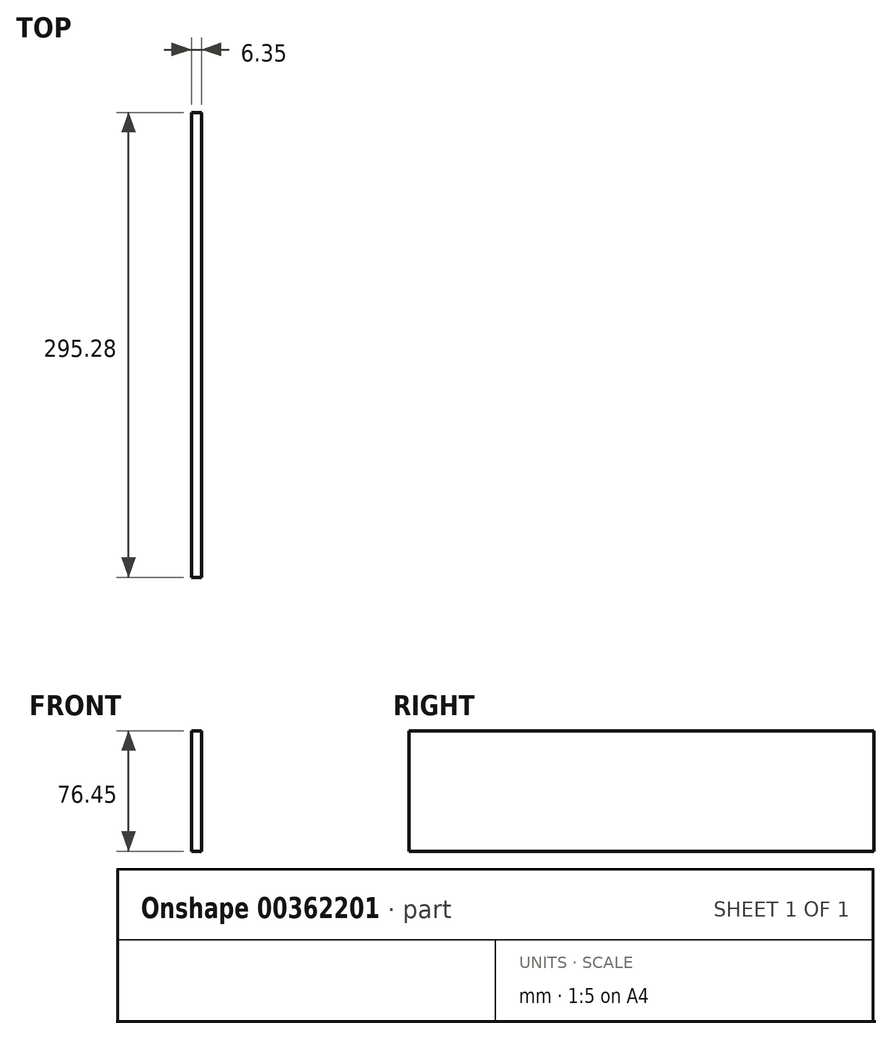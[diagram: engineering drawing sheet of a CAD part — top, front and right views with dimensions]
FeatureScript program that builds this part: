
annotation { "Feature Type Name" : "Feature", "Feature Type Description" : "" }
export const myFeature = defineFeature(function(context is Context, id is Id, definition is map)
    precondition{}
    {
        {
            var Q0;
            Q0=qCreatedBy(makeId("Right.planeOp"),FACE);
            var sketch = newSketch(context, id + "F0", { "sketchPlane" : qUnion([Q0])});
            skLineSegment(sketch, "E0.bottom", {"start": v(0, 0) * mm, "end": v(295.28, 0) * mm});
            skLineSegment(sketch, "E0.top", {"start": v(0, 76.45) * mm, "end": v(295.28, 76.45) * mm});
            skLineSegment(sketch, "E0.left", {"start": v(0, 0) * mm, "end": v(0, 76.45) * mm});
            skLineSegment(sketch, "E0.right", {"start": v(295.28, 0) * mm, "end": v(295.28, 76.45) * mm});
            skSolve(sketch);
        }
        {
            var Q0;
            Q0 = qSketchRegion(id + "F0", true);
            extrude(context, id + "F1", {"entities" : qUnion([Q0]), "depth" : 6.35 * mm, "offsetDistance" : 25.4 * mm});
        }
    });
